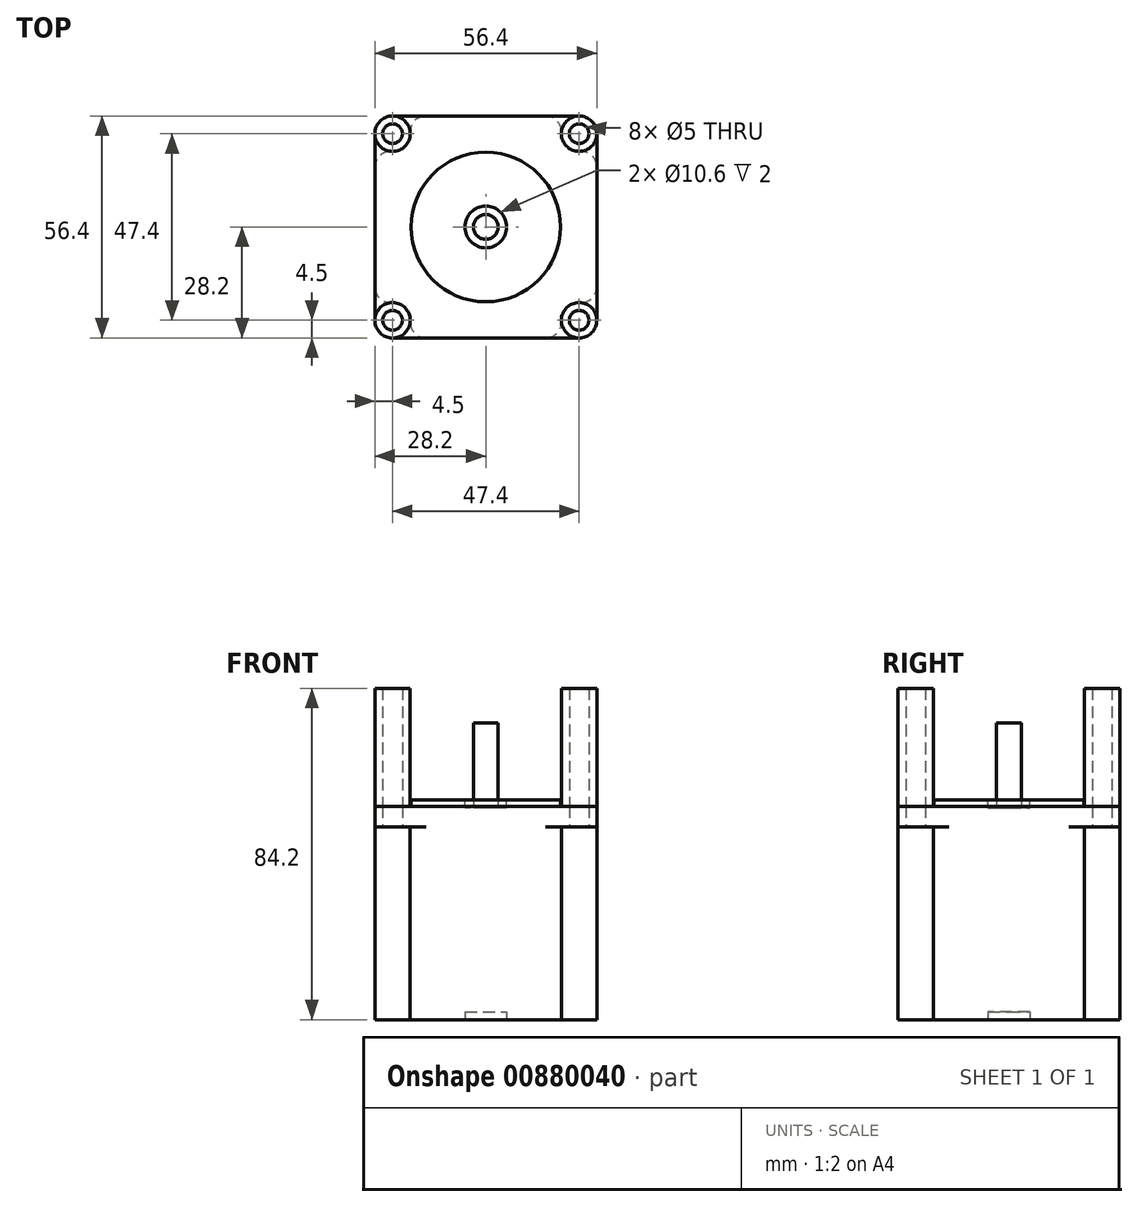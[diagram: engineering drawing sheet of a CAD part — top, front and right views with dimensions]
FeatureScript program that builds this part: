
annotation { "Feature Type Name" : "Feature", "Feature Type Description" : "" }
export const myFeature = defineFeature(function(context is Context, id is Id, definition is map)
    precondition{}
    {
        {
            var Q0;
            Q0=qCreatedBy(makeId("Top.planeOp"),FACE);
            var sketch = newSketch(context, id + "F0", { "sketchPlane" : qUnion([Q0])});
            skLineSegment(sketch, "E0.bottom", {"start": v(-23.7, 28.2) * mm, "end": v(23.7, 28.2) * mm});
            skLineSegment(sketch, "E0.top", {"start": v(-23.7, -28.2) * mm, "end": v(23.7, -28.2) * mm});
            skLineSegment(sketch, "E0.left", {"start": v(-28.2, 23.7) * mm, "end": v(-28.2, -23.7) * mm});
            skLineSegment(sketch, "E0.right", {"start": v(28.2, 23.7) * mm, "end": v(28.2, -23.7) * mm});
            skPoint(sketch, "E1.visualSharp", {"position": v(-28.2, 28.2) * mm});
            skArc(sketch, "E1.filletArc", {"start": v(-23.7, 28.2) * mm, "mid": v(-26.88, 26.88) * mm, "end": v(-28.2, 23.7) * mm});
            skPoint(sketch, "E2.visualSharp", {"position": v(28.2, 28.2) * mm});
            skArc(sketch, "E2.filletArc", {"start": v(28.2, 23.7) * mm, "mid": v(26.88, 26.88) * mm, "end": v(23.7, 28.2) * mm});
            skPoint(sketch, "E3.visualSharp", {"position": v(28.2, -28.2) * mm});
            skArc(sketch, "E3.filletArc", {"start": v(23.7, -28.2) * mm, "mid": v(26.88, -26.88) * mm, "end": v(28.2, -23.7) * mm});
            skPoint(sketch, "E4.visualSharp", {"position": v(-28.2, -28.2) * mm});
            skArc(sketch, "E4.filletArc", {"start": v(-28.2, -23.7) * mm, "mid": v(-26.88, -26.88) * mm, "end": v(-23.7, -28.2) * mm});
            skCircle(sketch, "E5", {"center": v(-23.7, -23.7) * mm, "radius": 2.5 * mm});
            skCircle(sketch, "E6", {"center": v(23.7, -23.7) * mm, "radius": 2.5 * mm});
            skCircle(sketch, "E7", {"center": v(-23.7, 23.7) * mm, "radius": 2.5 * mm});
            skCircle(sketch, "E8", {"center": v(23.7, 23.7) * mm, "radius": 2.5 * mm});
            skSolve(sketch);
        }
        {
            var Q0;
            Q0=makeQuery(id+"F0.imprint","IMPRINT",FACE,{"disambiguationData":[TD([[makeQuery(id+"F0.imprint","IMPRINT",EDGE,{"derivedFrom":sQuery(id+"F0.wireOp",EDGE,"E0.bottom")}),-1.0]])]});
            extrude(context, id + "F1", {"entities" : qUnion([Q0]), "depth" : 5.2 * mm});
        }
        {
            var Q0;
            Q0=makeQuery(id+"F1.opExtrude","CAP_FACE",FACE,{"disambiguationData":[OSD([sQuery(id+"F0.wireOp",EDGE,"E0.bottom"),sQuery(id+"F0.wireOp",EDGE,"E0.top"),sQuery(id+"F0.wireOp",EDGE,"E0.left"),sQuery(id+"F0.wireOp",EDGE,"E0.right"),sQuery(id+"F0.wireOp",EDGE,"E1.filletArc"),sQuery(id+"F0.wireOp",EDGE,"E2.filletArc"),sQuery(id+"F0.wireOp",EDGE,"E3.filletArc"),sQuery(id+"F0.wireOp",EDGE,"E4.filletArc"),sQuery(id+"F0.wireOp",EDGE,"E5"),sQuery(id+"F0.wireOp",EDGE,"E6"),sQuery(id+"F0.wireOp",EDGE,"E7"),sQuery(id+"F0.wireOp",EDGE,"E8")])],"isStart":true});
            var sketch = newSketch(context, id + "F2", { "sketchPlane" : qUnion([Q0])});
            skLineSegment(sketch, "E9.bottom", {"start": v(-15.21, -28.2) * mm, "end": v(15.21, -28.2) * mm});
            skLineSegment(sketch, "E9.top", {"start": v(-15.21, 28.2) * mm, "end": v(15.21, 28.2) * mm});
            skLineSegment(sketch, "E9.left", {"start": v(-28.2, -15.21) * mm, "end": v(-28.2, 15.21) * mm});
            skLineSegment(sketch, "E9.right", {"start": v(28.2, -15.21) * mm, "end": v(28.2, 15.21) * mm});
            skArc(sketch, "E10", {"start": v(-23.96, 19.2) * mm, "mid": v(-20.52, 20.52) * mm, "end": v(-19.2, 23.96) * mm});
            skArc(sketch, "E11", {"start": v(19.2, 23.96) * mm, "mid": v(20.52, 20.52) * mm, "end": v(23.96, 19.2) * mm});
            skArc(sketch, "E12", {"start": v(23.96, -19.2) * mm, "mid": v(20.52, -20.52) * mm, "end": v(19.2, -23.96) * mm});
            skArc(sketch, "E13", {"start": v(-19.2, -23.96) * mm, "mid": v(-20.52, -20.52) * mm, "end": v(-23.96, -19.2) * mm});
            skPoint(sketch, "E14.orphan", {"position": v(-28.2, -28.2) * mm});
            skPoint(sketch, "E15.orphan", {"position": v(28.2, 28.2) * mm});
            skPoint(sketch, "E16.visualSharp", {"position": v(-28.2, -23.7) * mm});
            skArc(sketch, "E16.filletArc", {"start": v(-28.2, -15.21) * mm, "mid": v(-26.94, -18.13) * mm, "end": v(-23.96, -19.2) * mm});
            skPoint(sketch, "E17.visualSharp", {"position": v(-23.7, -28.2) * mm});
            skArc(sketch, "E17.filletArc", {"start": v(-19.2, -23.96) * mm, "mid": v(-18.13, -26.94) * mm, "end": v(-15.21, -28.2) * mm});
            skPoint(sketch, "E18.visualSharp", {"position": v(23.7, -28.2) * mm});
            skArc(sketch, "E18.filletArc", {"start": v(15.21, -28.2) * mm, "mid": v(18.13, -26.94) * mm, "end": v(19.2, -23.96) * mm});
            skPoint(sketch, "E19.visualSharp", {"position": v(28.2, -23.7) * mm});
            skArc(sketch, "E19.filletArc", {"start": v(23.96, -19.2) * mm, "mid": v(26.94, -18.13) * mm, "end": v(28.2, -15.21) * mm});
            skPoint(sketch, "E20.visualSharp", {"position": v(28.2, 23.7) * mm});
            skArc(sketch, "E20.filletArc", {"start": v(28.2, 15.21) * mm, "mid": v(26.94, 18.13) * mm, "end": v(23.96, 19.2) * mm});
            skPoint(sketch, "E21.visualSharp", {"position": v(23.7, 28.2) * mm});
            skArc(sketch, "E21.filletArc", {"start": v(19.2, 23.96) * mm, "mid": v(18.13, 26.94) * mm, "end": v(15.21, 28.2) * mm});
            skPoint(sketch, "E22.visualSharp", {"position": v(-23.7, 28.2) * mm});
            skArc(sketch, "E22.filletArc", {"start": v(-15.21, 28.2) * mm, "mid": v(-18.13, 26.94) * mm, "end": v(-19.2, 23.96) * mm});
            skPoint(sketch, "E23.visualSharp", {"position": v(-28.2, 23.7) * mm});
            skArc(sketch, "E23.filletArc", {"start": v(-23.96, 19.2) * mm, "mid": v(-26.94, 18.13) * mm, "end": v(-28.2, 15.21) * mm});
            skSolve(sketch);
        }
        {
            var Q0;
            Q0=makeQuery(id+"F2.imprint","IMPRINT",FACE,{"disambiguationData":[TD([[makeQuery(id+"F2.imprint","IMPRINT",EDGE,{"derivedFrom":sQuery(id+"F2.wireOp",EDGE,"E9.bottom")}),1.0]])]});
            extrude(context, id + "F3", {"entities" : qUnion([Q0]), "operationType" : NewBodyOperationType.ADD, "depth" : 49 * mm});
        }
        {
            var Q0;
            Q0=makeQuery(id+"F1.opExtrude","CAP_FACE",FACE,{"disambiguationData":[OSD([sQuery(id+"F0.wireOp",EDGE,"E0.bottom"),sQuery(id+"F0.wireOp",EDGE,"E0.top"),sQuery(id+"F0.wireOp",EDGE,"E0.left"),sQuery(id+"F0.wireOp",EDGE,"E0.right"),sQuery(id+"F0.wireOp",EDGE,"E1.filletArc"),sQuery(id+"F0.wireOp",EDGE,"E2.filletArc"),sQuery(id+"F0.wireOp",EDGE,"E3.filletArc"),sQuery(id+"F0.wireOp",EDGE,"E4.filletArc"),sQuery(id+"F0.wireOp",EDGE,"E5"),sQuery(id+"F0.wireOp",EDGE,"E6"),sQuery(id+"F0.wireOp",EDGE,"E7"),sQuery(id+"F0.wireOp",EDGE,"E8")])],"isStart":false});
            var sketch = newSketch(context, id + "F4", { "sketchPlane" : qUnion([Q0])});
            skCircle(sketch, "E24", {"center": v(0, 0) * mm, "radius": 19 * mm});
            skSolve(sketch);
        }
        {
            var Q0;
            Q0=makeQuery(id+"F4.imprint","IMPRINT",FACE,{"disambiguationData":[TD([[makeQuery(id+"F4.imprint","IMPRINT",EDGE,{"derivedFrom":sQuery(id+"F4.wireOp",EDGE,"E24")}),1.0]])]});
            extrude(context, id + "F5", {"entities" : qUnion([Q0]), "operationType" : NewBodyOperationType.ADD, "depth" : 1.6 * mm});
        }
        {
            var Q0;
            Q0=makeQuery(id+"F5.opExtrude","CAP_FACE",FACE,{"disambiguationData":[OSD([sQuery(id+"F4.wireOp",EDGE,"E24")])],"isStart":false});
            var sketch = newSketch(context, id + "F6", { "sketchPlane" : qUnion([Q0])});
            skCircle(sketch, "E25", {"center": v(0, 0) * mm, "radius": 5.3 * mm});
            skSolve(sketch);
        }
        {
            var Q0;
            Q0=makeQuery(id+"F3.opExtrude","CAP_FACE",FACE,{"disambiguationData":[OSD([sQuery(id+"F2.wireOp",EDGE,"E9.bottom"),sQuery(id+"F2.wireOp",EDGE,"E9.top"),sQuery(id+"F2.wireOp",EDGE,"E9.left"),sQuery(id+"F2.wireOp",EDGE,"E9.right"),sQuery(id+"F2.wireOp",EDGE,"E10"),sQuery(id+"F2.wireOp",EDGE,"E11"),sQuery(id+"F2.wireOp",EDGE,"E12"),sQuery(id+"F2.wireOp",EDGE,"E13"),sQuery(id+"F2.wireOp",EDGE,"E16.filletArc"),sQuery(id+"F2.wireOp",EDGE,"E17.filletArc"),sQuery(id+"F2.wireOp",EDGE,"E18.filletArc"),sQuery(id+"F2.wireOp",EDGE,"E19.filletArc"),sQuery(id+"F2.wireOp",EDGE,"E20.filletArc"),sQuery(id+"F2.wireOp",EDGE,"E21.filletArc"),sQuery(id+"F2.wireOp",EDGE,"E22.filletArc"),sQuery(id+"F2.wireOp",EDGE,"E23.filletArc")])],"isStart":false});
            var sketch = newSketch(context, id + "F7", { "sketchPlane" : qUnion([Q0])});
            skCircle(sketch, "E26", {"center": v(0, 0) * mm, "radius": 5.3 * mm});
            skSolve(sketch);
        }
        {
            var Q0;
            Q0=makeQuery(id+"F6.imprint","IMPRINT",FACE,{"disambiguationData":[TD([[makeQuery(id+"F6.imprint","IMPRINT",EDGE,{"derivedFrom":sQuery(id+"F6.wireOp",EDGE,"E25")}),1.0]])]});
            extrude(context, id + "F8", {"entities" : qUnion([Q0]), "operationType" : NewBodyOperationType.REMOVE, "oppositeDirection" : true, "depth" : 2 * mm});
        }
        {
            var Q0;
            Q0=makeQuery(id+"F8.boolean.opBoolean","COPY",FACE,{"derivedFrom":makeQuery(id+"F8.opExtrude","CAP_FACE",FACE,{"disambiguationData":[OSD([sQuery(id+"F6.wireOp",EDGE,"E25")])],"isStart":false})});
            var sketch = newSketch(context, id + "F9", { "sketchPlane" : qUnion([Q0])});
            skCircle(sketch, "E27", {"center": v(0, 0) * mm, "radius": 3.15 * mm});
            skSolve(sketch);
        }
        {
            var Q0;
            Q0=makeQuery(id+"F9.imprint","IMPRINT",FACE,{"disambiguationData":[TD([[makeQuery(id+"F9.imprint","IMPRINT",EDGE,{"derivedFrom":sQuery(id+"F9.wireOp",EDGE,"E27")}),1.0]])]});
            extrude(context, id + "F10", {"entities" : qUnion([Q0]), "operationType" : NewBodyOperationType.ADD, "depth" : 21.6 * mm});
        }
        {
            var Q0;
            Q0=qSketchRegion(id+"F7",true);
            extrude(context, id + "F11", {"entities" : qUnion([Q0]), "operationType" : NewBodyOperationType.REMOVE, "oppositeDirection" : true, "depth" : 2 * mm});
        }
        {
            var Q0;
            Q0=makeQuery(id+"F1.opExtrude","CAP_FACE",FACE,{"disambiguationData":[OSD([sQuery(id+"F0.wireOp",EDGE,"E0.bottom"),sQuery(id+"F0.wireOp",EDGE,"E0.top"),sQuery(id+"F0.wireOp",EDGE,"E0.left"),sQuery(id+"F0.wireOp",EDGE,"E0.right"),sQuery(id+"F0.wireOp",EDGE,"E1.filletArc"),sQuery(id+"F0.wireOp",EDGE,"E2.filletArc"),sQuery(id+"F0.wireOp",EDGE,"E3.filletArc"),sQuery(id+"F0.wireOp",EDGE,"E4.filletArc"),sQuery(id+"F0.wireOp",EDGE,"E5"),sQuery(id+"F0.wireOp",EDGE,"E6"),sQuery(id+"F0.wireOp",EDGE,"E7"),sQuery(id+"F0.wireOp",EDGE,"E8")])],"isStart":false});
            var sketch = newSketch(context, id + "F12", { "sketchPlane" : qUnion([Q0])});
            skCircle(sketch, "E28", {"center": v(23.7, 23.7) * mm, "radius": 2.5 * mm});
            skCircle(sketch, "E29", {"center": v(-23.7, 23.7) * mm, "radius": 2.5 * mm});
            skCircle(sketch, "E30", {"center": v(-23.7, -23.7) * mm, "radius": 2.5 * mm});
            skCircle(sketch, "E31", {"center": v(23.7, -23.7) * mm, "radius": 2.5 * mm});
            skCircle(sketch, "E32", {"center": v(-23.7, 23.7) * mm, "radius": 4.5 * mm});
            skCircle(sketch, "E33", {"center": v(23.7, 23.7) * mm, "radius": 4.5 * mm});
            skCircle(sketch, "E34", {"center": v(23.7, -23.7) * mm, "radius": 4.5 * mm});
            skCircle(sketch, "E35", {"center": v(-23.7, -23.7) * mm, "radius": 4.5 * mm});
            skSolve(sketch);
        }
        {
            var Q0;
            Q0=makeQuery(id+"F12.imprint","IMPRINT",FACE,{"disambiguationData":[TD([[makeQuery(id+"F12.imprint","IMPRINT",EDGE,{"derivedFrom":sQuery(id+"F12.wireOp",EDGE,"E31")}),-1.0]])]});
            var Q1;
            Q1=makeQuery(id+"F12.imprint","IMPRINT",FACE,{"disambiguationData":[TD([[makeQuery(id+"F12.imprint","IMPRINT",EDGE,{"derivedFrom":sQuery(id+"F12.wireOp",EDGE,"E30")}),-1.0]])]});
            var Q2;
            Q2=makeQuery(id+"F12.imprint","IMPRINT",FACE,{"disambiguationData":[TD([[makeQuery(id+"F12.imprint","IMPRINT",EDGE,{"derivedFrom":sQuery(id+"F12.wireOp",EDGE,"E29")}),-1.0]])]});
            var Q3;
            Q3=makeQuery(id+"F12.imprint","IMPRINT",FACE,{"disambiguationData":[TD([[makeQuery(id+"F12.imprint","IMPRINT",EDGE,{"derivedFrom":sQuery(id+"F12.wireOp",EDGE,"E28")}),-1.0]])]});
            extrude(context, id + "F13", {"entities" : qUnion([Q0, Q1, Q2, Q3]), "depth" : 30 * mm});
        }
    });
